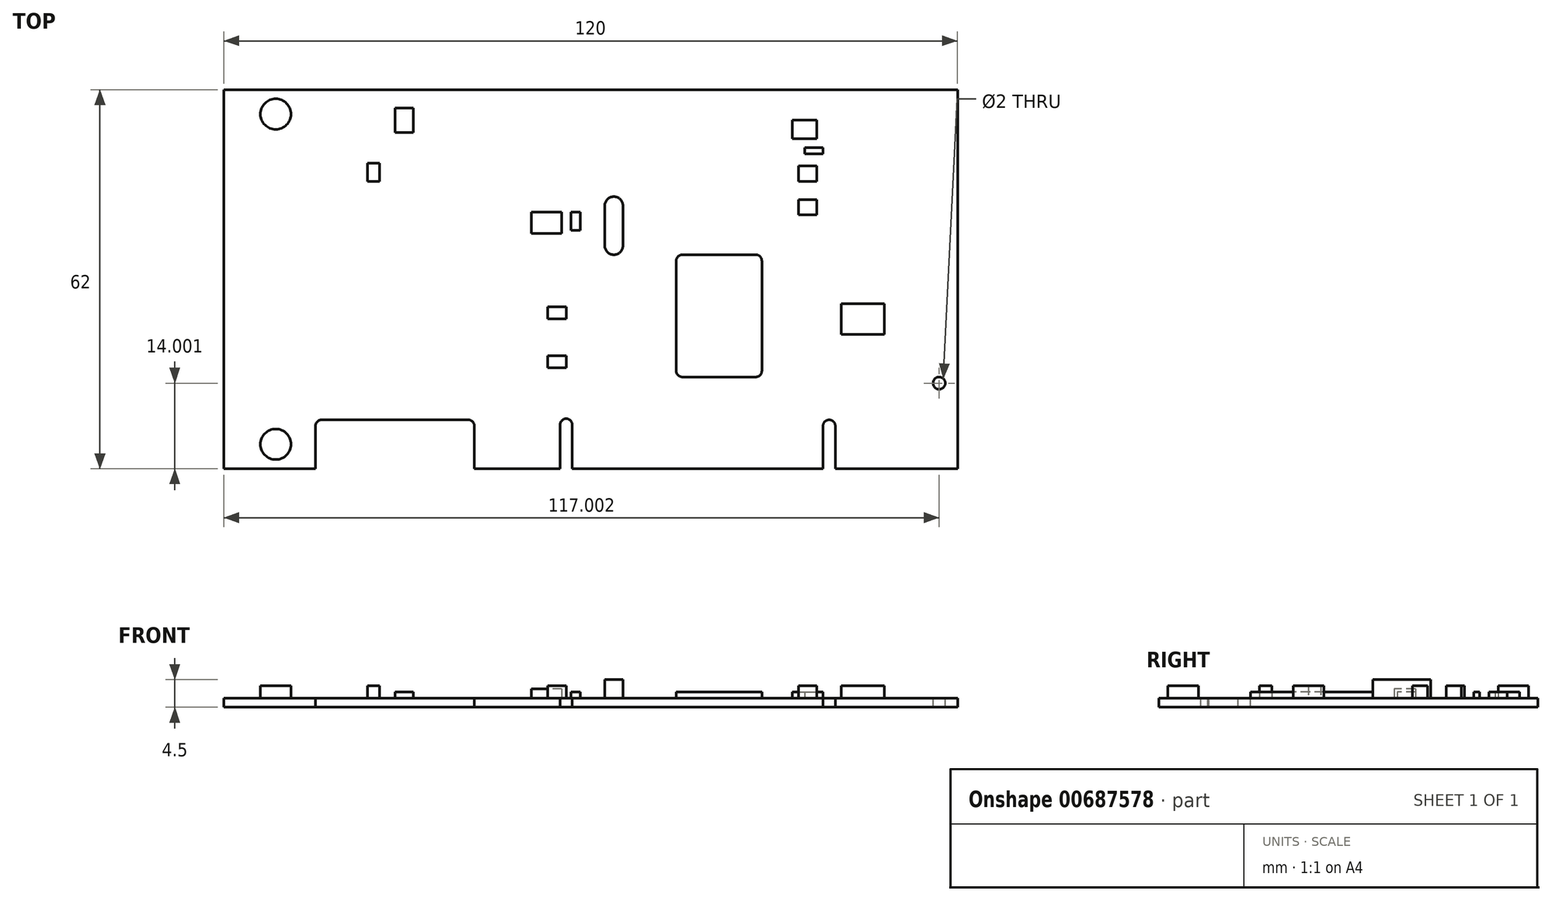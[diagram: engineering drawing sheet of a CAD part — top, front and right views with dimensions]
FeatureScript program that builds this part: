
annotation { "Feature Type Name" : "Feature", "Feature Type Description" : "" }
export const myFeature = defineFeature(function(context is Context, id is Id, definition is map)
    precondition{}
    {
        {
            var Q0;
            Q0=qCreatedBy(makeId("Top.planeOp"),FACE);
            var sketch = newSketch(context, id + "F0", { "sketchPlane" : qUnion([Q0])});
            skLineSegment(sketch, "E0.bottom", {"start": v(-61.14, 44.65) * mm, "end": v(58.86, 44.65) * mm});
            skLineSegment(sketch, "E0.top", {"start": v(-61.14, -17.35) * mm, "end": v(58.86, -17.35) * mm});
            skLineSegment(sketch, "E0.left", {"start": v(-61.14, 44.65) * mm, "end": v(-61.14, -17.35) * mm});
            skLineSegment(sketch, "E0.right", {"start": v(58.86, 44.65) * mm, "end": v(58.86, -17.35) * mm});
            skSolve(sketch);
        }
        {
            var Q0;
            Q0 = qSketchRegion(id + "F0", true);
            extrude(context, id + "F1", {"entities" : qUnion([Q0]), "depth" : 1.5 * mm, "offsetDistance" : 25 * mm});
        }
        {
            var Q0;
            Q0=makeQuery(id+"F1.opExtrude","CAP_FACE",FACE,{"disambiguationData":[OSD([sQuery(id+"F0.wireOp",EDGE,"E0.bottom"),sQuery(id+"F0.wireOp",EDGE,"E0.top"),sQuery(id+"F0.wireOp",EDGE,"E0.left"),sQuery(id+"F0.wireOp",EDGE,"E0.right")])],"isStart":false});
            var sketch = newSketch(context, id + "F2", { "sketchPlane" : qUnion([Q0])});
            skLineSegment(sketch, "E1", {"start": v(-46.14, -17.35) * mm, "end": v(-46.14, -10.35) * mm});
            skLineSegment(sketch, "E2", {"start": v(-45.14, -9.35) * mm, "end": v(-21.14, -9.35) * mm});
            skLineSegment(sketch, "E3", {"start": v(-20.14, -10.35) * mm, "end": v(-20.14, -17.35) * mm});
            skPoint(sketch, "E4.visualSharp", {"position": v(-46.14, -9.35) * mm});
            skArc(sketch, "E4.filletArc", {"start": v(-45.14, -9.35) * mm, "mid": v(-45.85, -9.64) * mm, "end": v(-46.14, -10.35) * mm});
            skPoint(sketch, "E5.visualSharp", {"position": v(-20.14, -9.35) * mm});
            skArc(sketch, "E5.filletArc", {"start": v(-20.14, -10.35) * mm, "mid": v(-20.43, -9.64) * mm, "end": v(-21.14, -9.35) * mm});
            skSolve(sketch);
        }
        {
            var Q0;
            Q0 = qSketchRegion(id + "F2", true);
            var Q1;
            {var subQ1=sQuery(id+"F2.wireOp",EDGE,"E1");Q1=makeQuery(id+"F2.imprint","IMPRINT",FACE,{"disambiguationData":[TD([[makeQuery(id+"F2.imprint","IMPRINT",EDGE,{"derivedFrom":subQ1}),-1.0]])]});}
            extrude(context, id + "F3", {"entities" : qUnion([Q0, Q1]), "operationType" : NewBodyOperationType.REMOVE, "endBound" : BoundingType.THROUGH_ALL, "oppositeDirection" : true, "depth" : 25 * mm, "offsetDistance" : 25 * mm});
        }
        {
            var Q0;
            Q0=makeQuery(id+"F1.opExtrude","CAP_FACE",FACE,{"disambiguationData":[OSD([sQuery(id+"F0.wireOp",EDGE,"E0.bottom"),sQuery(id+"F0.wireOp",EDGE,"E0.top"),sQuery(id+"F0.wireOp",EDGE,"E0.left"),sQuery(id+"F0.wireOp",EDGE,"E0.right")])],"isStart":false});
            var sketch = newSketch(context, id + "F4", { "sketchPlane" : qUnion([Q0])});
            skLineSegment(sketch, "E6", {"start": v(-6.14, -17.35) * mm, "end": v(-6.14, -10.16) * mm});
            skLineSegment(sketch, "E7", {"start": v(-4.14, -10.16) * mm, "end": v(-4.14, -17.35) * mm});
            skArc(sketch, "E8", {"start": v(-4.14, -10.16) * mm, "mid": v(-5.14, -9.16) * mm, "end": v(-6.14, -10.16) * mm});
            skPoint(sketch, "E9.orphan", {"position": v(-6.14, -9.35) * mm});
            skPoint(sketch, "E10.orphan", {"position": v(-4.14, -9.35) * mm});
            skSolve(sketch);
        }
        {
            var Q0;
            Q0 = qSketchRegion(id + "F4", true);
            var Q1;
            {var subQ0=sQuery(id+"F4.wireOp",EDGE,"E6");Q1=makeQuery(id+"F4.imprint","IMPRINT",FACE,{"disambiguationData":[TD([[makeQuery(id+"F4.imprint","IMPRINT",EDGE,{"derivedFrom":subQ0}),-1.0]])]});}
            extrude(context, id + "F5", {"entities" : qUnion([Q0, Q1]), "operationType" : NewBodyOperationType.REMOVE, "endBound" : BoundingType.THROUGH_ALL, "oppositeDirection" : true, "depth" : 25 * mm, "offsetDistance" : 25 * mm});
        }
        {
            var Q0;
            Q0=makeQuery(id+"F1.opExtrude","CAP_FACE",FACE,{"disambiguationData":[OSD([sQuery(id+"F0.wireOp",EDGE,"E0.bottom"),sQuery(id+"F0.wireOp",EDGE,"E0.top"),sQuery(id+"F0.wireOp",EDGE,"E0.left"),sQuery(id+"F0.wireOp",EDGE,"E0.right")])],"isStart":false});
            var sketch = newSketch(context, id + "F6", { "sketchPlane" : qUnion([Q0])});
            skLineSegment(sketch, "E11", {"start": v(38.86, -10.23) * mm, "end": v(38.86, -17.35) * mm});
            skArc(sketch, "E12", {"start": v(38.86, -10.47) * mm, "mid": v(37.87, -9.35) * mm, "end": v(36.88, -10.46) * mm});
            skPoint(sketch, "E13.orphan", {"position": v(38.86, -9.35) * mm});
            skPoint(sketch, "E14", {"position": v(36.88, -10.23) * mm});
            skPoint(sketch, "E15.end.orphan", {"position": v(36.86, -9.35) * mm});
            skPoint(sketch, "E15.start.orphan", {"position": v(36.86, -17.35) * mm});
            skLineSegment(sketch, "E16", {"start": v(36.88, -10.23) * mm, "end": v(36.86, -17.35) * mm});
            skSolve(sketch);
        }
        {
            var Q0;
            Q0 = qSketchRegion(id + "F6", true);
            var Q1;
            {var subQ0=sQuery(id+"F6.wireOp",EDGE,"E12");var subQ1=sQuery(id+"F6.wireOp",EDGE,"E11");var subQ2=makeQuery(id+"F6.imprint","INTERSECT",VERTEX,{"disambiguationData":[OD(0.0)],"derivedFrom":[subQ1,subQ0]});Q1=makeQuery(id+"F6.imprint","IMPRINT",FACE,{"disambiguationData":[TD([[makeQuery(id+"F6.imprint","IMPRINT",EDGE,{"disambiguationData":[TD([[subQ2,-1.0]])],"derivedFrom":subQ1}),-1.0]])]});}
            extrude(context, id + "F7", {"entities" : qUnion([Q0, Q1]), "operationType" : NewBodyOperationType.REMOVE, "endBound" : BoundingType.THROUGH_ALL, "oppositeDirection" : true, "depth" : 25 * mm, "offsetDistance" : 25 * mm});
        }
        {
            var Q0;
            Q0=makeQuery(id+"F1.opExtrude","CAP_FACE",FACE,{"disambiguationData":[OSD([sQuery(id+"F0.wireOp",EDGE,"E0.bottom"),sQuery(id+"F0.wireOp",EDGE,"E0.top"),sQuery(id+"F0.wireOp",EDGE,"E0.left"),sQuery(id+"F0.wireOp",EDGE,"E0.right")])],"isStart":false});
            var sketch = newSketch(context, id + "F8", { "sketchPlane" : qUnion([Q0])});
            skCircle(sketch, "E17", {"center": v(55.86, -3.35) * mm, "radius": 1 * mm});
            skSolve(sketch);
        }
        {
            var Q0;
            Q0 = qSketchRegion(id + "F8", true);
            extrude(context, id + "F9", {"entities" : qUnion([Q0]), "operationType" : NewBodyOperationType.REMOVE, "endBound" : BoundingType.THROUGH_ALL, "oppositeDirection" : true, "depth" : 25 * mm, "offsetDistance" : 25 * mm});
        }
        {
            var Q0;
            Q0=makeQuery(id+"F1.opExtrude","CAP_FACE",FACE,{"disambiguationData":[OSD([sQuery(id+"F0.wireOp",EDGE,"E0.bottom"),sQuery(id+"F0.wireOp",EDGE,"E0.top"),sQuery(id+"F0.wireOp",EDGE,"E0.left"),sQuery(id+"F0.wireOp",EDGE,"E0.right")])],"isStart":false});
            var sketch = newSketch(context, id + "F10", { "sketchPlane" : qUnion([Q0])});
            skLineSegment(sketch, "E18.bottom", {"start": v(39.86, 9.65) * mm, "end": v(46.86, 9.65) * mm});
            skLineSegment(sketch, "E18.top", {"start": v(39.86, 4.65) * mm, "end": v(46.86, 4.65) * mm});
            skLineSegment(sketch, "E18.left", {"start": v(39.86, 9.65) * mm, "end": v(39.86, 4.65) * mm});
            skLineSegment(sketch, "E18.right", {"start": v(46.86, 9.65) * mm, "end": v(46.86, 4.65) * mm});
            skSolve(sketch);
        }
        {
            var Q0;
            Q0 = qSketchRegion(id + "F10", true);
            extrude(context, id + "F11", {"entities" : qUnion([Q0]), "operationType" : NewBodyOperationType.ADD, "depth" : 2 * mm, "offsetDistance" : 25 * mm});
        }
        {
            var Q0;
            Q0=makeQuery(id+"F1.opExtrude","CAP_FACE",FACE,{"disambiguationData":[OSD([sQuery(id+"F0.wireOp",EDGE,"E0.bottom"),sQuery(id+"F0.wireOp",EDGE,"E0.top"),sQuery(id+"F0.wireOp",EDGE,"E0.left"),sQuery(id+"F0.wireOp",EDGE,"E0.right")])],"isStart":false});
            var sketch = newSketch(context, id + "F12", { "sketchPlane" : qUnion([Q0])});
            skLineSegment(sketch, "E19.bottom", {"start": v(13.86, 17.65) * mm, "end": v(25.86, 17.65) * mm});
            skLineSegment(sketch, "E19.top", {"start": v(13.86, -2.35) * mm, "end": v(25.86, -2.35) * mm});
            skLineSegment(sketch, "E19.left", {"start": v(12.86, 16.65) * mm, "end": v(12.86, -1.35) * mm});
            skLineSegment(sketch, "E19.right", {"start": v(26.86, 16.65) * mm, "end": v(26.86, -1.35) * mm});
            skPoint(sketch, "E20.visualSharp", {"position": v(12.86, 17.65) * mm});
            skArc(sketch, "E20.filletArc", {"start": v(13.86, 17.65) * mm, "mid": v(13.15, 17.36) * mm, "end": v(12.86, 16.65) * mm});
            skPoint(sketch, "E21.visualSharp", {"position": v(26.86, 17.65) * mm});
            skArc(sketch, "E21.filletArc", {"start": v(26.86, 16.65) * mm, "mid": v(26.57, 17.36) * mm, "end": v(25.86, 17.65) * mm});
            skPoint(sketch, "E22.visualSharp", {"position": v(12.86, -2.35) * mm});
            skArc(sketch, "E22.filletArc", {"start": v(12.86, -1.35) * mm, "mid": v(13.15, -2.06) * mm, "end": v(13.86, -2.35) * mm});
            skPoint(sketch, "E23.visualSharp", {"position": v(26.86, -2.35) * mm});
            skArc(sketch, "E23.filletArc", {"start": v(25.86, -2.35) * mm, "mid": v(26.57, -2.06) * mm, "end": v(26.86, -1.35) * mm});
            skSolve(sketch);
        }
        {
            var Q0;
            Q0 = qSketchRegion(id + "F12", true);
            extrude(context, id + "F13", {"entities" : qUnion([Q0]), "operationType" : NewBodyOperationType.ADD, "depth" : 1 * mm, "offsetDistance" : 25 * mm});
        }
        {
            var Q0;
            Q0=makeQuery(id+"F1.opExtrude","CAP_FACE",FACE,{"disambiguationData":[OSD([sQuery(id+"F0.wireOp",EDGE,"E0.bottom"),sQuery(id+"F0.wireOp",EDGE,"E0.top"),sQuery(id+"F0.wireOp",EDGE,"E0.left"),sQuery(id+"F0.wireOp",EDGE,"E0.right")])],"isStart":false});
            var sketch = newSketch(context, id + "F14", { "sketchPlane" : qUnion([Q0])});
            skLineSegment(sketch, "E24.bottom", {"start": v(32.86, 26.65) * mm, "end": v(35.86, 26.65) * mm});
            skLineSegment(sketch, "E24.top", {"start": v(32.86, 24.15) * mm, "end": v(35.86, 24.15) * mm});
            skLineSegment(sketch, "E24.left", {"start": v(32.86, 26.65) * mm, "end": v(32.86, 24.15) * mm});
            skLineSegment(sketch, "E24.right", {"start": v(35.86, 26.65) * mm, "end": v(35.86, 24.15) * mm});
            skSolve(sketch);
        }
        {
            var Q0;
            Q0 = qSketchRegion(id + "F14", true);
            extrude(context, id + "F15", {"entities" : qUnion([Q0]), "operationType" : NewBodyOperationType.ADD, "depth" : 2 * mm, "offsetDistance" : 25 * mm});
        }
        {
            var Q0;
            Q0=makeQuery(id+"F1.opExtrude","CAP_FACE",FACE,{"disambiguationData":[OSD([sQuery(id+"F0.wireOp",EDGE,"E0.bottom"),sQuery(id+"F0.wireOp",EDGE,"E0.top"),sQuery(id+"F0.wireOp",EDGE,"E0.left"),sQuery(id+"F0.wireOp",EDGE,"E0.right")])],"isStart":false});
            var sketch = newSketch(context, id + "F16", { "sketchPlane" : qUnion([Q0])});
            skLineSegment(sketch, "E25.bottom", {"start": v(32.86, 32.15) * mm, "end": v(35.86, 32.15) * mm});
            skLineSegment(sketch, "E25.top", {"start": v(32.86, 29.65) * mm, "end": v(35.86, 29.65) * mm});
            skLineSegment(sketch, "E25.left", {"start": v(32.86, 32.15) * mm, "end": v(32.86, 29.65) * mm});
            skLineSegment(sketch, "E25.right", {"start": v(35.86, 32.15) * mm, "end": v(35.86, 29.65) * mm});
            skSolve(sketch);
        }
        {
            var Q0;
            Q0 = qSketchRegion(id + "F16", true);
            extrude(context, id + "F17", {"entities" : qUnion([Q0]), "operationType" : NewBodyOperationType.ADD, "depth" : 2 * mm, "offsetDistance" : 25 * mm});
        }
        {
            var Q0;
            Q0=makeQuery(id+"F1.opExtrude","CAP_FACE",FACE,{"disambiguationData":[OSD([sQuery(id+"F0.wireOp",EDGE,"E0.bottom"),sQuery(id+"F0.wireOp",EDGE,"E0.top"),sQuery(id+"F0.wireOp",EDGE,"E0.left"),sQuery(id+"F0.wireOp",EDGE,"E0.right")])],"isStart":false});
            var sketch = newSketch(context, id + "F18", { "sketchPlane" : qUnion([Q0])});
            skLineSegment(sketch, "E26.bottom", {"start": v(33.86, 35.15) * mm, "end": v(36.86, 35.15) * mm});
            skLineSegment(sketch, "E26.top", {"start": v(33.86, 34.15) * mm, "end": v(36.86, 34.15) * mm});
            skLineSegment(sketch, "E26.left", {"start": v(33.86, 35.15) * mm, "end": v(33.86, 34.15) * mm});
            skLineSegment(sketch, "E26.right", {"start": v(36.86, 35.15) * mm, "end": v(36.86, 34.15) * mm});
            skSolve(sketch);
        }
        {
            var Q0;
            Q0 = qSketchRegion(id + "F18", true);
            extrude(context, id + "F19", {"entities" : qUnion([Q0]), "operationType" : NewBodyOperationType.ADD, "depth" : 1 * mm, "offsetDistance" : 25 * mm});
        }
        {
            var Q0;
            Q0=makeQuery(id+"F1.opExtrude","CAP_FACE",FACE,{"disambiguationData":[OSD([sQuery(id+"F0.wireOp",EDGE,"E0.bottom"),sQuery(id+"F0.wireOp",EDGE,"E0.top"),sQuery(id+"F0.wireOp",EDGE,"E0.left"),sQuery(id+"F0.wireOp",EDGE,"E0.right")])],"isStart":false});
            var sketch = newSketch(context, id + "F20", { "sketchPlane" : qUnion([Q0])});
            skLineSegment(sketch, "E27.bottom", {"start": v(31.86, 39.65) * mm, "end": v(35.86, 39.65) * mm});
            skLineSegment(sketch, "E27.top", {"start": v(31.86, 36.65) * mm, "end": v(35.86, 36.65) * mm});
            skLineSegment(sketch, "E27.left", {"start": v(31.86, 39.65) * mm, "end": v(31.86, 36.65) * mm});
            skLineSegment(sketch, "E27.right", {"start": v(35.86, 39.65) * mm, "end": v(35.86, 36.65) * mm});
            skSolve(sketch);
        }
        {
            var Q0;
            Q0 = qSketchRegion(id + "F20", true);
            extrude(context, id + "F21", {"entities" : qUnion([Q0]), "operationType" : NewBodyOperationType.ADD, "depth" : 1 * mm, "offsetDistance" : 25 * mm});
        }
        {
            var Q0;
            Q0=makeQuery(id+"F1.opExtrude","CAP_FACE",FACE,{"disambiguationData":[OSD([sQuery(id+"F0.wireOp",EDGE,"E0.bottom"),sQuery(id+"F0.wireOp",EDGE,"E0.top"),sQuery(id+"F0.wireOp",EDGE,"E0.left"),sQuery(id+"F0.wireOp",EDGE,"E0.right")])],"isStart":false});
            var sketch = newSketch(context, id + "F22", { "sketchPlane" : qUnion([Q0])});
            skLineSegment(sketch, "E28.bottom", {"start": v(2.65, 27.15) * mm, "end": v(2.65, 27.15) * mm});
            skLineSegment(sketch, "E28.top", {"start": v(2.65, 17.65) * mm, "end": v(2.65, 17.65) * mm});
            skLineSegment(sketch, "E28.left", {"start": v(1.15, 25.65) * mm, "end": v(1.15, 19.15) * mm});
            skLineSegment(sketch, "E28.right", {"start": v(4.15, 25.65) * mm, "end": v(4.15, 19.15) * mm});
            skPoint(sketch, "E29.visualSharp", {"position": v(4.15, 27.15) * mm});
            skArc(sketch, "E29.filletArc", {"start": v(4.15, 25.65) * mm, "mid": v(3.72, 26.71) * mm, "end": v(2.65, 27.15) * mm});
            skPoint(sketch, "E30.visualSharp", {"position": v(1.15, 27.15) * mm});
            skArc(sketch, "E30.filletArc", {"start": v(2.65, 27.15) * mm, "mid": v(1.6, 26.71) * mm, "end": v(1.15, 25.65) * mm});
            skPoint(sketch, "E31.visualSharp", {"position": v(4.15, 17.65) * mm});
            skArc(sketch, "E31.filletArc", {"start": v(2.65, 17.65) * mm, "mid": v(3.72, 18.1) * mm, "end": v(4.15, 19.15) * mm});
            skPoint(sketch, "E32.visualSharp", {"position": v(1.15, 17.65) * mm});
            skArc(sketch, "E32.filletArc", {"start": v(1.15, 19.15) * mm, "mid": v(1.6, 18.1) * mm, "end": v(2.65, 17.65) * mm});
            skSolve(sketch);
        }
        {
            var Q0;
            Q0=makeQuery(id+"F22.imprint","IMPRINT",FACE,{"disambiguationData":[TD([[makeQuery(id+"F22.imprint","IMPRINT",EDGE,{"derivedFrom":sQuery(id+"F22.wireOp",EDGE,"E28.left")}),1.0]])]});
            extrude(context, id + "F23", {"entities" : qUnion([Q0]), "operationType" : NewBodyOperationType.ADD, "depth" : 3 * mm, "offsetDistance" : 25 * mm});
        }
        {
            var Q0;
            Q0=makeQuery(id+"F1.opExtrude","CAP_FACE",FACE,{"disambiguationData":[OSD([sQuery(id+"F0.wireOp",EDGE,"E0.bottom"),sQuery(id+"F0.wireOp",EDGE,"E0.top"),sQuery(id+"F0.wireOp",EDGE,"E0.left"),sQuery(id+"F0.wireOp",EDGE,"E0.right")])],"isStart":false});
            var sketch = newSketch(context, id + "F24", { "sketchPlane" : qUnion([Q0])});
            skLineSegment(sketch, "E33.bottom", {"start": v(-2.85, 24.65) * mm, "end": v(-4.35, 24.65) * mm});
            skLineSegment(sketch, "E33.top", {"start": v(-2.85, 21.65) * mm, "end": v(-4.35, 21.65) * mm});
            skLineSegment(sketch, "E33.left", {"start": v(-2.85, 24.65) * mm, "end": v(-2.85, 21.65) * mm});
            skLineSegment(sketch, "E33.right", {"start": v(-4.35, 24.65) * mm, "end": v(-4.35, 21.65) * mm});
            skSolve(sketch);
        }
        {
            var Q0;
            Q0 = qSketchRegion(id + "F24", true);
            extrude(context, id + "F25", {"entities" : qUnion([Q0]), "operationType" : NewBodyOperationType.ADD, "depth" : 1 * mm, "offsetDistance" : 25 * mm});
        }
        {
            var Q0;
            Q0=makeQuery(id+"F1.opExtrude","CAP_FACE",FACE,{"disambiguationData":[OSD([sQuery(id+"F0.wireOp",EDGE,"E0.bottom"),sQuery(id+"F0.wireOp",EDGE,"E0.top"),sQuery(id+"F0.wireOp",EDGE,"E0.left"),sQuery(id+"F0.wireOp",EDGE,"E0.right")])],"isStart":false});
            var sketch = newSketch(context, id + "F26", { "sketchPlane" : qUnion([Q0])});
            skLineSegment(sketch, "E34.bottom", {"start": v(-5.85, 24.65) * mm, "end": v(-10.85, 24.65) * mm});
            skLineSegment(sketch, "E34.top", {"start": v(-5.85, 21.15) * mm, "end": v(-10.85, 21.15) * mm});
            skLineSegment(sketch, "E34.left", {"start": v(-5.85, 24.65) * mm, "end": v(-5.85, 21.15) * mm});
            skLineSegment(sketch, "E34.right", {"start": v(-10.85, 24.65) * mm, "end": v(-10.85, 21.15) * mm});
            skSolve(sketch);
        }
        {
            var Q0;
            Q0 = qSketchRegion(id + "F26", true);
            extrude(context, id + "F27", {"entities" : qUnion([Q0]), "operationType" : NewBodyOperationType.ADD, "depth" : 1.5 * mm, "offsetDistance" : 25 * mm});
        }
        {
            var Q0;
            Q0=makeQuery(id+"F1.opExtrude","CAP_FACE",FACE,{"disambiguationData":[OSD([sQuery(id+"F0.wireOp",EDGE,"E0.bottom"),sQuery(id+"F0.wireOp",EDGE,"E0.top"),sQuery(id+"F0.wireOp",EDGE,"E0.left"),sQuery(id+"F0.wireOp",EDGE,"E0.right")])],"isStart":false});
            var sketch = newSketch(context, id + "F28", { "sketchPlane" : qUnion([Q0])});
            skLineSegment(sketch, "E35.bottom", {"start": v(-5.14, 9.15) * mm, "end": v(-8.14, 9.15) * mm});
            skLineSegment(sketch, "E35.top", {"start": v(-5.14, 7.15) * mm, "end": v(-8.14, 7.15) * mm});
            skLineSegment(sketch, "E35.left", {"start": v(-5.14, 9.15) * mm, "end": v(-5.14, 7.15) * mm});
            skLineSegment(sketch, "E35.right", {"start": v(-8.14, 9.15) * mm, "end": v(-8.14, 7.15) * mm});
            skSolve(sketch);
        }
        {
            var Q0;
            Q0 = qSketchRegion(id + "F28", true);
            extrude(context, id + "F29", {"entities" : qUnion([Q0]), "operationType" : NewBodyOperationType.ADD, "depth" : 2 * mm, "offsetDistance" : 25 * mm});
        }
        {
            var Q0;
            Q0=makeQuery(id+"F1.opExtrude","CAP_FACE",FACE,{"disambiguationData":[OSD([sQuery(id+"F0.wireOp",EDGE,"E0.bottom"),sQuery(id+"F0.wireOp",EDGE,"E0.top"),sQuery(id+"F0.wireOp",EDGE,"E0.left"),sQuery(id+"F0.wireOp",EDGE,"E0.right")])],"isStart":false});
            var sketch = newSketch(context, id + "F30", { "sketchPlane" : qUnion([Q0])});
            skLineSegment(sketch, "E36.bottom", {"start": v(-5.14, 1.15) * mm, "end": v(-8.14, 1.15) * mm});
            skLineSegment(sketch, "E36.top", {"start": v(-5.14, -0.85) * mm, "end": v(-8.14, -0.85) * mm});
            skLineSegment(sketch, "E36.left", {"start": v(-5.14, 1.15) * mm, "end": v(-5.14, -0.85) * mm});
            skLineSegment(sketch, "E36.right", {"start": v(-8.14, 1.15) * mm, "end": v(-8.14, -0.85) * mm});
            skSolve(sketch);
        }
        {
            var Q0;
            Q0=makeQuery(id+"F30.imprint","IMPRINT",FACE,{"disambiguationData":[TD([[makeQuery(id+"F30.imprint","IMPRINT",EDGE,{"derivedFrom":sQuery(id+"F30.wireOp",EDGE,"E36.bottom")}),1.0]])]});
            extrude(context, id + "F31", {"entities" : qUnion([Q0]), "operationType" : NewBodyOperationType.ADD, "depth" : 2 * mm, "offsetDistance" : 25 * mm});
        }
        {
            var Q0;
            Q0=makeQuery(id+"F1.opExtrude","CAP_FACE",FACE,{"disambiguationData":[OSD([sQuery(id+"F0.wireOp",EDGE,"E0.bottom"),sQuery(id+"F0.wireOp",EDGE,"E0.top"),sQuery(id+"F0.wireOp",EDGE,"E0.left"),sQuery(id+"F0.wireOp",EDGE,"E0.right")])],"isStart":false});
            var sketch = newSketch(context, id + "F32", { "sketchPlane" : qUnion([Q0])});
            skCircle(sketch, "E37", {"center": v(-52.64, 40.65) * mm, "radius": 2.5 * mm});
            skSolve(sketch);
        }
        {
            var Q0;
            Q0 = qSketchRegion(id + "F32", true);
            extrude(context, id + "F33", {"entities" : qUnion([Q0]), "operationType" : NewBodyOperationType.ADD, "depth" : 2 * mm, "offsetDistance" : 25 * mm});
        }
        {
            var Q0;
            Q0=makeQuery(id+"F1.opExtrude","CAP_FACE",FACE,{"disambiguationData":[OSD([sQuery(id+"F0.wireOp",EDGE,"E0.bottom"),sQuery(id+"F0.wireOp",EDGE,"E0.top"),sQuery(id+"F0.wireOp",EDGE,"E0.left"),sQuery(id+"F0.wireOp",EDGE,"E0.right")])],"isStart":false});
            var sketch = newSketch(context, id + "F34", { "sketchPlane" : qUnion([Q0])});
            skCircle(sketch, "E38", {"center": v(-52.64, -13.35) * mm, "radius": 2.5 * mm});
            skSolve(sketch);
        }
        {
            var Q0;
            Q0 = qSketchRegion(id + "F34", true);
            extrude(context, id + "F35", {"entities" : qUnion([Q0]), "operationType" : NewBodyOperationType.ADD, "depth" : 2 * mm, "offsetDistance" : 25 * mm});
        }
        {
            var Q0;
            Q0=makeQuery(id+"F1.opExtrude","CAP_FACE",FACE,{"disambiguationData":[OSD([sQuery(id+"F0.wireOp",EDGE,"E0.bottom"),sQuery(id+"F0.wireOp",EDGE,"E0.top"),sQuery(id+"F0.wireOp",EDGE,"E0.left"),sQuery(id+"F0.wireOp",EDGE,"E0.right")])],"isStart":false});
            var sketch = newSketch(context, id + "F36", { "sketchPlane" : qUnion([Q0])});
            skLineSegment(sketch, "E39.bottom", {"start": v(-33.14, 41.65) * mm, "end": v(-30.14, 41.65) * mm});
            skLineSegment(sketch, "E39.top", {"start": v(-33.14, 37.65) * mm, "end": v(-30.14, 37.65) * mm});
            skLineSegment(sketch, "E39.left", {"start": v(-33.14, 41.65) * mm, "end": v(-33.14, 37.65) * mm});
            skLineSegment(sketch, "E39.right", {"start": v(-30.14, 41.65) * mm, "end": v(-30.14, 37.65) * mm});
            skSolve(sketch);
        }
        {
            var Q0;
            Q0 = qSketchRegion(id + "F36", true);
            extrude(context, id + "F37", {"entities" : qUnion([Q0]), "operationType" : NewBodyOperationType.ADD, "depth" : 1 * mm, "offsetDistance" : 25 * mm});
        }
        {
            var Q0;
            Q0=makeQuery(id+"F1.opExtrude","CAP_FACE",FACE,{"disambiguationData":[OSD([sQuery(id+"F0.wireOp",EDGE,"E0.bottom"),sQuery(id+"F0.wireOp",EDGE,"E0.top"),sQuery(id+"F0.wireOp",EDGE,"E0.left"),sQuery(id+"F0.wireOp",EDGE,"E0.right")])],"isStart":false});
            var sketch = newSketch(context, id + "F38", { "sketchPlane" : qUnion([Q0])});
            skLineSegment(sketch, "E40.bottom", {"start": v(-37.64, 32.65) * mm, "end": v(-35.64, 32.65) * mm});
            skLineSegment(sketch, "E40.top", {"start": v(-37.64, 29.65) * mm, "end": v(-35.64, 29.65) * mm});
            skLineSegment(sketch, "E40.left", {"start": v(-37.64, 32.65) * mm, "end": v(-37.64, 29.65) * mm});
            skLineSegment(sketch, "E40.right", {"start": v(-35.64, 32.65) * mm, "end": v(-35.64, 29.65) * mm});
            skSolve(sketch);
        }
        {
            var Q0;
            Q0 = qSketchRegion(id + "F38", true);
            extrude(context, id + "F39", {"entities" : qUnion([Q0]), "operationType" : NewBodyOperationType.ADD, "depth" : 2 * mm, "offsetDistance" : 25 * mm});
        }
    });
